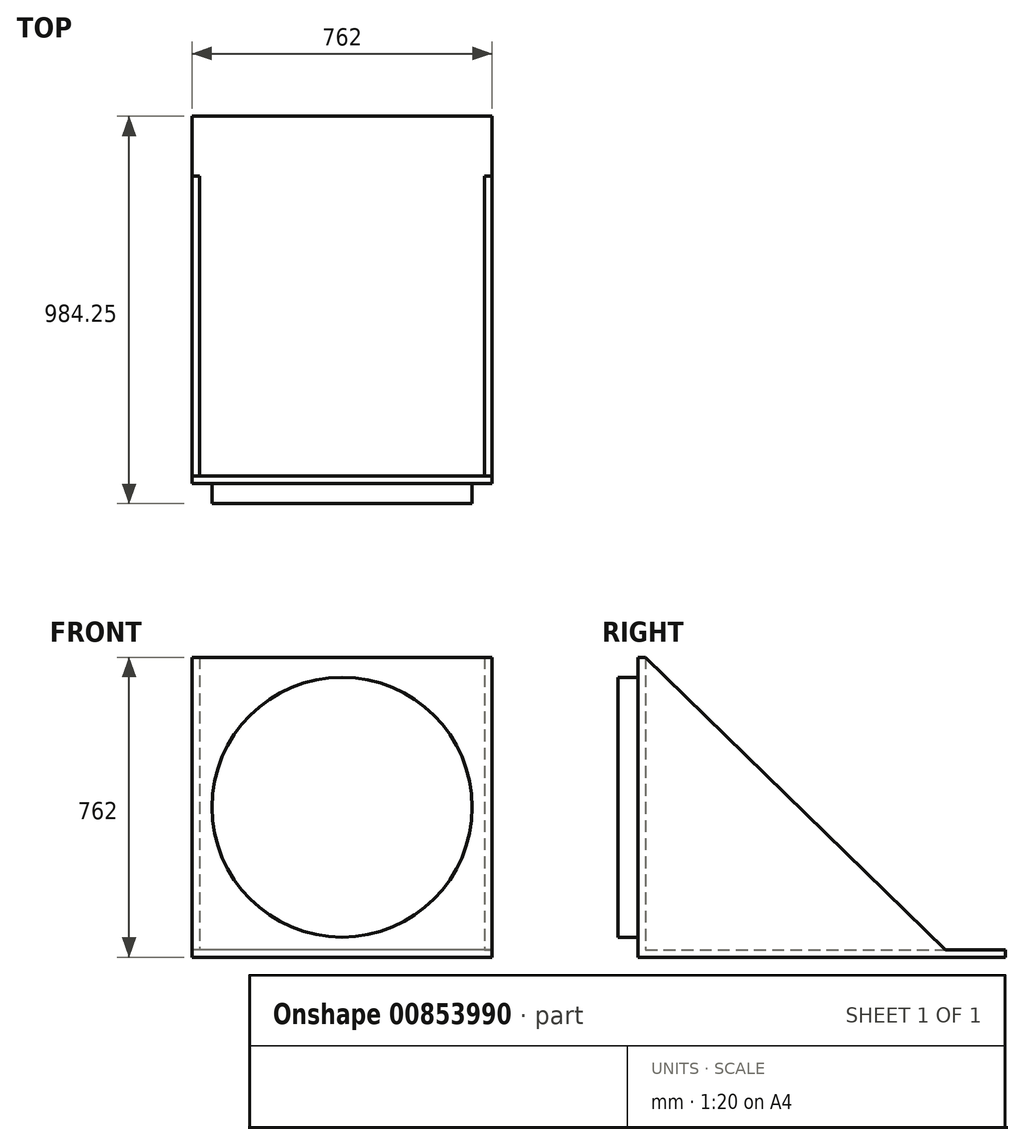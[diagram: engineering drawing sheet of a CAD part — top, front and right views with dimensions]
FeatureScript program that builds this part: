
annotation { "Feature Type Name" : "Feature", "Feature Type Description" : "" }
export const myFeature = defineFeature(function(context is Context, id is Id, definition is map)
    precondition{}
    {
        {
            var Q0;
            Q0=qCreatedBy(makeId("Front.planeOp"),FACE);
            var sketch = newSketch(context, id + "F0", { "sketchPlane" : qUnion([Q0])});
            skLineSegment(sketch, "E0.bottom", {"start": v(381, 381) * mm, "end": v(-381, 381) * mm});
            skLineSegment(sketch, "E0.top", {"start": v(381, -381) * mm, "end": v(-381, -381) * mm});
            skLineSegment(sketch, "E0.left", {"start": v(381, 381) * mm, "end": v(381, -381) * mm});
            skLineSegment(sketch, "E0.right", {"start": v(-381, 381) * mm, "end": v(-381, -381) * mm});
            skPoint(sketch, "E0.middle", {"position": v(0, 0) * mm});
            skSolve(sketch);
        }
        {
            var Q0;
            Q0 = qSketchRegion(id + "F0", true);
            extrude(context, id + "F1", {"entities" : qUnion([Q0]), "depth" : 19.05 * mm, "offsetDistance" : 25.4 * mm});
        }
        {
            var Q0;
            Q0=makeQuery(id+"F1.opExtrude","SWEPT_FACE",FACE,{"disambiguationData":[OSD([sQuery(id+"F0.wireOp",EDGE,"E0.top")])]});
            var sketch = newSketch(context, id + "F2", { "sketchPlane" : qUnion([Q0])});
            skLineSegment(sketch, "E1.bottom", {"start": v(381, 0) * mm, "end": v(-381, 0) * mm});
            skLineSegment(sketch, "E1.top", {"start": v(381, -914.4) * mm, "end": v(-381, -914.4) * mm});
            skLineSegment(sketch, "E1.left", {"start": v(381, 0) * mm, "end": v(381, -914.4) * mm});
            skLineSegment(sketch, "E1.right", {"start": v(-381, 0) * mm, "end": v(-381, -914.4) * mm});
            skSolve(sketch);
        }
        {
            var Q0;
            Q0 = qSketchRegion(id + "F2", true);
            extrude(context, id + "F3", {"entities" : qUnion([Q0]), "operationType" : NewBodyOperationType.ADD, "depth" : -19.05 * mm, "offsetDistance" : 25.4 * mm});
        }
        {
            var Q0;
            Q0=makeQuery(id+"F3.boolean.opBoolean","MERGE",FACE,{"derivedFrom":[makeQuery(id+"F1.opExtrude","SWEPT_FACE",FACE,{"disambiguationData":[OSD([sQuery(id+"F0.wireOp",EDGE,"E0.right")])]}),makeQuery(id+"F3.opExtrude","SWEPT_FACE",FACE,{"disambiguationData":[OSD([sQuery(id+"F2.wireOp",EDGE,"E1.right")])]})]});
            var sketch = newSketch(context, id + "F4", { "sketchPlane" : qUnion([Q0])});
            skLineSegment(sketch, "E2", {"start": v(0, 381) * mm, "end": v(0, -361.95) * mm});
            skLineSegment(sketch, "E3", {"start": v(0, -361.95) * mm, "end": v(-762, -361.95) * mm});
            skLineSegment(sketch, "E4", {"start": v(-762, -361.95) * mm, "end": v(0, 381) * mm});
            skLineSegment(sketch, "E5", {"start": v(0, -361.95) * mm, "end": v(-635, -361.95) * mm});
            skLineSegment(sketch, "E6", {"start": v(-635, -361.95) * mm, "end": v(0, 257.18) * mm});
            skLineSegment(sketch, "E7", {"start": v(0, 273.05) * mm, "end": v(0, -361.95) * mm});
            skSolve(sketch);
        }
        {
            var Q0;
            Q0 = qSketchRegion(id + "F4", true);
            extrude(context, id + "F5", {"entities" : qUnion([Q0]), "operationType" : NewBodyOperationType.ADD, "depth" : -19.05 * mm, "offsetDistance" : 25.4 * mm});
        }
        {
            var Q0;
            Q0=makeQuery(id+"F3.boolean.opBoolean","MERGE",FACE,{"derivedFrom":[makeQuery(id+"F1.opExtrude","SWEPT_FACE",FACE,{"disambiguationData":[OSD([sQuery(id+"F0.wireOp",EDGE,"E0.left")])]}),makeQuery(id+"F3.opExtrude","SWEPT_FACE",FACE,{"disambiguationData":[OSD([sQuery(id+"F2.wireOp",EDGE,"E1.left")])]})]});
            var sketch = newSketch(context, id + "F6", { "sketchPlane" : qUnion([Q0])});
            skLineSegment(sketch, "E8", {"start": v(0, -361.95) * mm, "end": v(0, 381) * mm});
            skLineSegment(sketch, "E9", {"start": v(0, 381) * mm, "end": v(762, -361.95) * mm});
            skLineSegment(sketch, "E10", {"start": v(762, -361.95) * mm, "end": v(0, -361.95) * mm});
            skSolve(sketch);
        }
        {
            var Q0;
            Q0 = qSketchRegion(id + "F6", true);
            extrude(context, id + "F7", {"entities" : qUnion([Q0]), "operationType" : NewBodyOperationType.ADD, "depth" : -19.05 * mm, "offsetDistance" : 25.4 * mm});
        }
        {
            var Q0;
            Q0=makeQuery(id+"F1.opExtrude","CAP_FACE",FACE,{"disambiguationData":[OSD([sQuery(id+"F0.wireOp",EDGE,"E0.bottom"),sQuery(id+"F0.wireOp",EDGE,"E0.top"),sQuery(id+"F0.wireOp",EDGE,"E0.left"),sQuery(id+"F0.wireOp",EDGE,"E0.right")])],"isStart":false});
            var sketch = newSketch(context, id + "F8", { "sketchPlane" : qUnion([Q0])});
            skCircle(sketch, "E11", {"center": v(0, 0) * mm, "radius": 330.2 * mm});
            skSolve(sketch);
        }
        {
            var Q0;
            Q0 = qSketchRegion(id + "F8", true);
            extrude(context, id + "F9", {"entities" : qUnion([Q0]), "operationType" : NewBodyOperationType.ADD, "depth" : 50.8 * mm, "offsetDistance" : 25.4 * mm});
        }
    });
